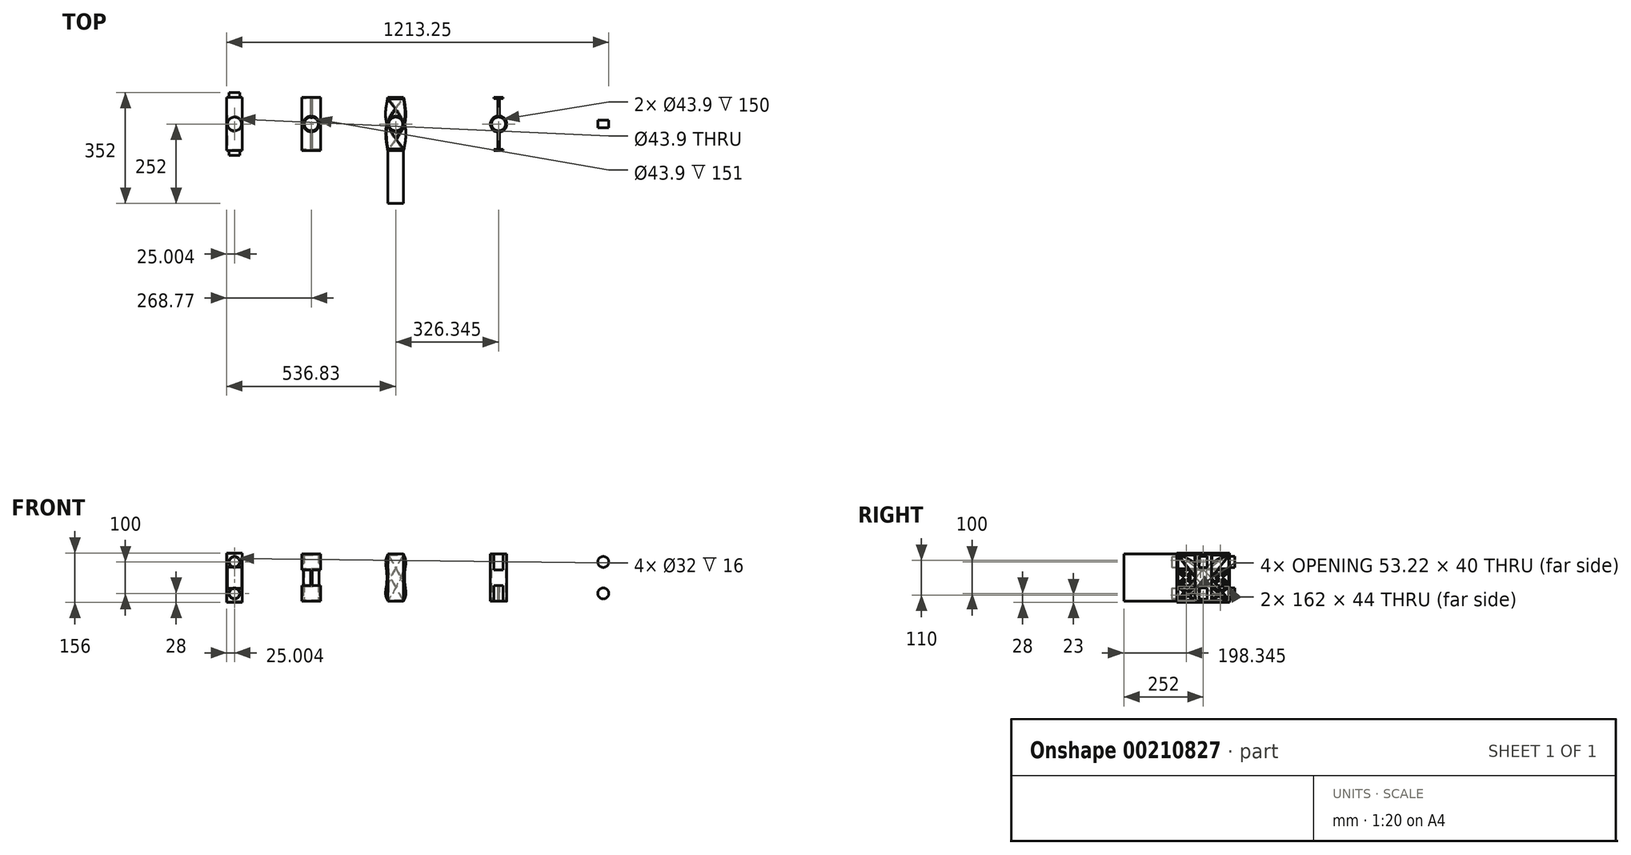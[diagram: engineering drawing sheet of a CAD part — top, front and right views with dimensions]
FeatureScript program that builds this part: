
annotation { "Feature Type Name" : "Feature", "Feature Type Description" : "" }
export const myFeature = defineFeature(function(context is Context, id is Id, definition is map)
    precondition{}
    {
        {
            var Q0;
            Q0=qCreatedBy(makeId("Top.planeOp"),FACE);
            var sketch = newSketch(context, id + "F0", { "sketchPlane" : qUnion([Q0])});
            skCircle(sketch, "E0", {"center": v(363.02, 0) * mm, "radius": 21.95 * mm});
            skCircle(sketch, "E1.0", {"center": v(363.02, 0) * mm, "radius": 25 * mm});
            skLineSegment(sketch, "E2", {"start": v(363.02, 131.9) * mm, "end": v(363.02, -84) * mm, "construction": true});
            skLineSegment(sketch, "E3", {"start": v(363.02, -84) * mm, "end": v(388.02, -84) * mm});
            skLineSegment(sketch, "E4", {"start": v(388.02, -84) * mm, "end": v(388.02, 0) * mm});
            skLineSegment(sketch, "E5.MirrorCS", {"start": v(363.02, -84) * mm, "end": v(338.02, -84) * mm});
            skLineSegment(sketch, "E6.MirrorCS", {"start": v(338.02, -84) * mm, "end": v(338.02, 0) * mm});
            skLineSegment(sketch, "E7", {"start": v(0, 0) * mm, "end": v(451.55, 0) * mm, "construction": true});
            skLineSegment(sketch, "E8.MirrorCS", {"start": v(388.02, 84) * mm, "end": v(388.02, 0) * mm});
            skLineSegment(sketch, "E9.MirrorCS", {"start": v(363.02, 84) * mm, "end": v(388.02, 84) * mm});
            skLineSegment(sketch, "E10.MirrorCS", {"start": v(363.02, 84) * mm, "end": v(338.02, 84) * mm});
            skLineSegment(sketch, "E11.MirrorCS", {"start": v(338.02, 84) * mm, "end": v(338.02, 0) * mm});
            skLineSegment(sketch, "E12.0", {"start": v(363.02, 82) * mm, "end": v(386.02, 82) * mm});
            skLineSegment(sketch, "E12.1", {"start": v(363.02, 82) * mm, "end": v(340.02, 82) * mm});
            skLineSegment(sketch, "E12.2", {"start": v(386.02, 82) * mm, "end": v(386.02, 0) * mm});
            skLineSegment(sketch, "E12.3", {"start": v(340.02, 82) * mm, "end": v(340.02, 0) * mm});
            skLineSegment(sketch, "E12.4", {"start": v(386.02, -82) * mm, "end": v(386.02, 0) * mm});
            skLineSegment(sketch, "E12.5", {"start": v(363.02, -82) * mm, "end": v(386.02, -82) * mm});
            skLineSegment(sketch, "E12.6", {"start": v(363.02, -82) * mm, "end": v(340.02, -82) * mm});
            skLineSegment(sketch, "E12.7", {"start": v(340.02, -82) * mm, "end": v(340.02, 0) * mm});
            skSolve(sketch);
        }
        {
            var Q0;
            Q0=sQuery(id+"F0.wireOp",EDGE,"E2");
            var Q1;
            Q1=sQuery(id+"F0.wireOp",VERTEX,"E5.MirrorCS.start");
            cPlane(context, id + "F1", {"entities" : qUnion([Q0, Q1]), "cplaneType" : CPlaneType.LINE_POINT, "offset" : 25 * mm, "width" : 150 * mm, "height" : 150 * mm});
        }
        {
            var Q0;
            Q0=qCreatedBy(id+"F1.planeOp",FACE);
            var sketch = newSketch(context, id + "F2", { "sketchPlane" : qUnion([Q0])});
            skLineSegment(sketch, "E13.bottom", {"start": v(338.02, 150) * mm, "end": v(388.02, 150) * mm});
            skLineSegment(sketch, "E13.top", {"start": v(338.02, 0) * mm, "end": v(388.02, 0) * mm});
            skLineSegment(sketch, "E13.left", {"start": v(338.02, 150) * mm, "end": v(338.02, 0) * mm});
            skLineSegment(sketch, "E13.right", {"start": v(388.02, 150) * mm, "end": v(388.02, 0) * mm});
            skLineSegment(sketch, "E14", {"start": v(363.02, -41.72) * mm, "end": v(363.02, 175.72) * mm, "construction": true});
            skCircle(sketch, "E15", {"center": v(363.02, 25) * mm, "radius": 17.5 * mm});
            skCircle(sketch, "E16", {"center": v(363.02, 125) * mm, "radius": 17.5 * mm});
            skSolve(sketch);
        }
        {
            var Q0;
            {var subQ0=sQuery(id+"F0.wireOp",EDGE,"E9.MirrorCS");Q0=makeQuery(id+"F0.imprint","IMPRINT",FACE,{"disambiguationData":[TD([[makeQuery(id+"F0.imprint","IMPRINT",EDGE,{"derivedFrom":subQ0}),-1.0]])]});}
            var Q1;
            Q1=makeQuery(id+"F0.imprint","IMPRINT",FACE,{"disambiguationData":[TD([[makeQuery(id+"F0.imprint","IMPRINT",EDGE,{"derivedFrom":sQuery(id+"F0.wireOp",EDGE,"E0")}),-1.0]])]});
            var Q2;
            {var subQ3=sQuery(id+"F0.wireOp",EDGE,"E1.0");var subQ7=makeQuery(id+"F0.imprint","INTERSECT",VERTEX,{"derivedFrom":[subQ3,sQuery(id+"F0.wireOp",EDGE,"E11.MirrorCS")]});Q2=makeQuery(id+"F0.imprint","IMPRINT",FACE,{"disambiguationData":[TD([[makeQuery(id+"F0.imprint","IMPRINT",EDGE,{"disambiguationData":[TD([[subQ7,1.0]])],"derivedFrom":subQ3}),1.0]])]});}
            var Q3;
            {var subQ3=sQuery(id+"F0.wireOp",EDGE,"E1.0");var subQ5=makeQuery(id+"F0.imprint","INTERSECT",VERTEX,{"derivedFrom":[subQ3,sQuery(id+"F0.wireOp",EDGE,"E8.MirrorCS")]});Q3=makeQuery(id+"F0.imprint","IMPRINT",FACE,{"disambiguationData":[TD([[makeQuery(id+"F0.imprint","IMPRINT",EDGE,{"disambiguationData":[TD([[subQ5,-1.0]])],"derivedFrom":subQ3}),1.0]])]});}
            var Q4;
            {var subQ1=sQuery(id+"F0.wireOp",EDGE,"E3");Q4=makeQuery(id+"F0.imprint","IMPRINT",FACE,{"disambiguationData":[TD([[makeQuery(id+"F0.imprint","IMPRINT",EDGE,{"derivedFrom":subQ1}),1.0]])]});}
            var Q5;
            Q5=sQuery(id+"F2.wireOp",VERTEX,"E13.left.start");
            extrude(context, id + "F3", {"entities" : qUnion([Q0, Q1, Q2, Q3, Q4]), "endBound" : BoundingType.UP_TO_VERTEX, "endBoundEntityVertex" : qUnion([Q5]), "depth" : 25 * mm});
        }
        {
            var Q0;
            Q0=makeQuery(id+"F2.imprint","IMPRINT",FACE,{"disambiguationData":[TD([[makeQuery(id+"F2.imprint","IMPRINT",EDGE,{"derivedFrom":sQuery(id+"F2.wireOp",EDGE,"E16")}),1.0]])]});
            var Q1;
            Q1=makeQuery(id+"F2.imprint","IMPRINT",FACE,{"disambiguationData":[TD([[makeQuery(id+"F2.imprint","IMPRINT",EDGE,{"derivedFrom":sQuery(id+"F2.wireOp",EDGE,"E15")}),1.0]])]});
            extrude(context, id + "F4", {"entities" : qUnion([Q0, Q1]), "depth" : 16 * mm});
        }
        {
            var Q0;
            Q0=qCreatedBy(makeId("Front.planeOp"),FACE);
            var sketch = newSketch(context, id + "F5", { "sketchPlane" : qUnion([Q0])});
            skLineSegment(sketch, "E17", {"start": v(363.02, 230.87) * mm, "end": v(363.02, -116.23) * mm, "construction": true});
            skSolve(sketch);
        }
        {
            var Q0;
            Q0=sQuery(id+"F2.wireOp",VERTEX,"E15.center");
            var Q1;
            Q1=sQuery(id+"F2.wireOp",VERTEX,"E16.center");
            var Q2;
            Q2=makeQuery(id+"F4.opExtrude","SWEPT_BODY",BODY,{"disambiguationData":[OSD([sQuery(id+"F2.wireOp",EDGE,"E16")])]});
            var Q3;
            Q3=makeQuery(id+"F4.opExtrude","SWEPT_BODY",BODY,{"disambiguationData":[OSD([sQuery(id+"F2.wireOp",EDGE,"E15")])]});
            hole(context, id + "F6", {"style" : HoleStyle.SIMPLE, "endStyle" : HoleEndStyle.THROUGH, "oppositeDirection" : true, "holeDiameter" : 32 * mm, "locations" : qUnion([Q0, Q1]), "scope" : qUnion([Q2, Q3]), "isTappedThrough" : true});
        }
        {
            var Q0;
            Q0=makeQuery(id+"F4.opExtrude","SWEPT_BODY",BODY,{"disambiguationData":[OSD([sQuery(id+"F2.wireOp",EDGE,"E16")])]});
            var Q1;
            Q1=makeQuery(id+"F4.opExtrude","SWEPT_BODY",BODY,{"disambiguationData":[OSD([sQuery(id+"F2.wireOp",EDGE,"E15")])]});
            var Q2;
            Q2=qCreatedBy(makeId("Front.planeOp"),FACE);
            mirror(context, id + "F7", {"operationType" : NewBodyOperationType.ADD, "entities" : qUnion([Q0, Q1]), "mirrorPlane" : qUnion([Q2])});
        }
        {
            var Q0;
            Q0=qCreatedBy(makeId("Top.planeOp"),FACE);
            var sketch = newSketch(context, id + "F8", { "sketchPlane" : qUnion([Q0])});
            skLineSegment(sketch, "E18", {"start": v(354.9, 0) * mm, "end": v(696.57, 0) * mm, "construction": true});
            skLineSegment(sketch, "E19", {"start": v(606.79, 88.82) * mm, "end": v(606.79, 0) * mm, "construction": true});
            skLineSegment(sketch, "E20", {"start": v(606.79, 0) * mm, "end": v(606.79, -110.58) * mm, "construction": true});
            skCircle(sketch, "E21", {"center": v(606.79, 0) * mm, "radius": 21.95 * mm});
            skCircle(sketch, "E22", {"center": v(606.79, 0) * mm, "radius": 25 * mm});
            skLineSegment(sketch, "E23.bottom", {"start": v(636.79, -84) * mm, "end": v(576.79, -84) * mm});
            skLineSegment(sketch, "E23.top", {"start": v(636.79, 84) * mm, "end": v(576.79, 84) * mm});
            skLineSegment(sketch, "E23.left", {"start": v(636.79, -84) * mm, "end": v(636.79, 84) * mm});
            skLineSegment(sketch, "E23.right", {"start": v(576.79, -84) * mm, "end": v(576.79, 84) * mm});
            skLineSegment(sketch, "E24.bottom", {"start": v(636.79, 84) * mm, "end": v(661.79, 84) * mm});
            skLineSegment(sketch, "E24.top", {"start": v(636.79, -84) * mm, "end": v(661.79, -84) * mm});
            skLineSegment(sketch, "E24.left", {"start": v(636.79, 84) * mm, "end": v(636.79, -84) * mm});
            skLineSegment(sketch, "E24.right", {"start": v(661.79, 84) * mm, "end": v(661.79, -84) * mm});
            skPoint(sketch, "E24.middle", {"position": v(649.29, 0) * mm});
            skSolve(sketch);
        }
        {
            var Q0;
            Q0=sQuery(id+"F8.wireOp",EDGE,"E23.right");
            var Q1;
            Q1=qCreatedBy(makeId("Right.planeOp"),FACE);
            cPlane(context, id + "F9", {"entities" : qUnion([Q0, Q1]), "cplaneType" : CPlaneType.LINE_ANGLE, "offset" : 25 * mm, "angle" : 0 * degree, "width" : 150 * mm, "height" : 150 * mm});
        }
        {
            var Q0;
            Q0=qCreatedBy(id+"F9.planeOp",FACE);
            var sketch = newSketch(context, id + "F10", { "sketchPlane" : qUnion([Q0])});
            skLineSegment(sketch, "E25", {"start": v(0, 0) * mm, "end": v(0, 324.05) * mm, "construction": true});
            skLineSegment(sketch, "E26.bottom", {"start": v(-84, 50) * mm, "end": v(84, 50) * mm});
            skLineSegment(sketch, "E26.top", {"start": v(-84, 0) * mm, "end": v(84, 0) * mm});
            skLineSegment(sketch, "E26.left", {"start": v(-84, 50) * mm, "end": v(-84, 0) * mm});
            skLineSegment(sketch, "E26.right", {"start": v(84, 50) * mm, "end": v(84, 0) * mm});
            skPoint(sketch, "E26.middle", {"position": v(0, 25) * mm});
            skLineSegment(sketch, "E27.bottom", {"start": v(-84, 100) * mm, "end": v(84, 100) * mm});
            skLineSegment(sketch, "E27.left", {"start": v(-84, 100) * mm, "end": v(-84, 50) * mm});
            skLineSegment(sketch, "E27.right", {"start": v(84, 100) * mm, "end": v(84, 50) * mm});
            skPoint(sketch, "E27.middle", {"position": v(0, 75) * mm});
            skLineSegment(sketch, "E28.bottom", {"start": v(-84, 150) * mm, "end": v(84, 150) * mm});
            skLineSegment(sketch, "E28.left", {"start": v(-84, 150) * mm, "end": v(-84, 100) * mm});
            skLineSegment(sketch, "E28.right", {"start": v(84, 150) * mm, "end": v(84, 100) * mm});
            skPoint(sketch, "E28.middle", {"position": v(0, 125) * mm});
            skLineSegment(sketch, "E29.bottom", {"start": v(-81, 3) * mm, "end": v(81, 3) * mm});
            skLineSegment(sketch, "E29.top", {"start": v(-81, 47) * mm, "end": v(81, 47) * mm});
            skLineSegment(sketch, "E29.left", {"start": v(-81, 3) * mm, "end": v(-81, 47) * mm});
            skLineSegment(sketch, "E29.right", {"start": v(81, 3) * mm, "end": v(81, 47) * mm});
            skLineSegment(sketch, "E30.bottom", {"start": v(-81, 103) * mm, "end": v(81, 103) * mm});
            skLineSegment(sketch, "E30.top", {"start": v(-81, 147) * mm, "end": v(81, 147) * mm});
            skLineSegment(sketch, "E30.left", {"start": v(-81, 103) * mm, "end": v(-81, 147) * mm});
            skLineSegment(sketch, "E30.right", {"start": v(81, 103) * mm, "end": v(81, 147) * mm});
            skSolve(sketch);
        }
        {
            var Q0;
            Q0=makeQuery(id+"F10.imprint","IMPRINT",FACE,{"disambiguationData":[TD([[makeQuery(id+"F10.imprint","IMPRINT",EDGE,{"derivedFrom":sQuery(id+"F10.wireOp",EDGE,"E28.bottom")}),-1.0]])]});
            var Q1;
            Q1=makeQuery(id+"F10.imprint","IMPRINT",FACE,{"disambiguationData":[TD([[makeQuery(id+"F10.imprint","IMPRINT",EDGE,{"derivedFrom":sQuery(id+"F10.wireOp",EDGE,"E26.top")}),1.0]])]});
            var Q2;
            Q2=sQuery(id+"F8.wireOp",VERTEX,"E24.top.start");
            extrude(context, id + "F11", {"entities" : qUnion([Q0, Q1]), "endBound" : BoundingType.UP_TO_VERTEX, "oppositeDirection" : true, "endBoundEntityVertex" : qUnion([Q2]), "depth" : 25 * mm});
        }
        {
            var Q0;
            Q0=makeQuery(id+"F8.imprint","IMPRINT",FACE,{"disambiguationData":[TD([[makeQuery(id+"F8.imprint","IMPRINT",EDGE,{"derivedFrom":sQuery(id+"F8.wireOp",EDGE,"E21")}),-1.0]])]});
            var Q1;
            Q1=makeQuery(id+"F11.opExtrude","CAP_VERTEX",VERTEX,{"disambiguationData":[OSD([sQuery(id+"F10.wireOp",EDGE,"E28.bottom"),sQuery(id+"F10.wireOp",EDGE,"E28.right"),dummyQuery(id+"F11.vertexPlane.planeOp",FACE)])],"isStart":false});
            extrude(context, id + "F12", {"entities" : qUnion([Q0]), "operationType" : NewBodyOperationType.ADD, "endBoundEntityVertex" : qUnion([Q1]), "depth" : 151 * mm});
        }
        {
            var Q0;
            Q0=makeQuery(id+"F8.imprint","IMPRINT",FACE,{"disambiguationData":[TD([[makeQuery(id+"F8.imprint","IMPRINT",EDGE,{"derivedFrom":sQuery(id+"F8.wireOp",EDGE,"E21")}),1.0]])]});
            extrude(context, id + "F13", {"entities" : qUnion([Q0]), "operationType" : NewBodyOperationType.REMOVE, "depth" : 151 * mm});
        }
        {
            var Q0;
            Q0=sQuery(id+"F8.wireOp",EDGE,"E20");
            var Q1;
            Q1=qCreatedBy(makeId("Right.planeOp"),FACE);
            cPlane(context, id + "F14", {"entities" : qUnion([Q0, Q1]), "cplaneType" : CPlaneType.LINE_ANGLE, "offset" : 25 * mm, "angle" : 0 * degree, "width" : 150 * mm, "height" : 150 * mm});
        }
        {
            var Q0;
            Q0=qCreatedBy(id+"F14.planeOp",FACE);
            var sketch = newSketch(context, id + "F15", { "sketchPlane" : qUnion([Q0])});
            skLineSegment(sketch, "E31", {"start": v(84, 100) * mm, "end": v(23.18, 48.45) * mm, "construction": true});
            skLineSegment(sketch, "E32", {"start": v(84, 50) * mm, "end": v(23.18, 104.08) * mm, "construction": true});
            skLineSegment(sketch, "E33", {"start": v(84, 100) * mm, "end": v(79, 100) * mm});
            skLineSegment(sketch, "E34", {"start": v(79, 100) * mm, "end": v(55.65, 80.2) * mm});
            skLineSegment(sketch, "E35", {"start": v(55.65, 80.2) * mm, "end": v(33.39, 100) * mm});
            skLineSegment(sketch, "E36", {"start": v(33.39, 100) * mm, "end": v(22.77, 100) * mm});
            skLineSegment(sketch, "E37", {"start": v(22.77, 100) * mm, "end": v(50.2, 75.6) * mm});
            skLineSegment(sketch, "E38", {"start": v(50.2, 75.6) * mm, "end": v(20, 50) * mm});
            skLineSegment(sketch, "E39", {"start": v(20, 50) * mm, "end": v(30.9, 50) * mm});
            skLineSegment(sketch, "E40", {"start": v(30.9, 50) * mm, "end": v(55.53, 70.87) * mm});
            skLineSegment(sketch, "E41", {"start": v(55.53, 70.87) * mm, "end": v(79, 50) * mm});
            skLineSegment(sketch, "E42", {"start": v(79, 50) * mm, "end": v(84, 50) * mm});
            skLineSegment(sketch, "E43", {"start": v(84, 50) * mm, "end": v(84, 55) * mm});
            skLineSegment(sketch, "E44", {"start": v(84, 55) * mm, "end": v(60.97, 75.48) * mm});
            skLineSegment(sketch, "E45", {"start": v(60.97, 75.48) * mm, "end": v(84, 95) * mm});
            skLineSegment(sketch, "E46", {"start": v(84, 95) * mm, "end": v(84, 100) * mm});
            skSolve(sketch);
        }
        {
            var Q0;
            Q0=makeQuery(id+"F15.imprint","IMPRINT",FACE,{"disambiguationData":[TD([[makeQuery(id+"F15.imprint","IMPRINT",EDGE,{"derivedFrom":sQuery(id+"F15.wireOp",EDGE,"E33")}),1.0]])]});
            extrude(context, id + "F16", {"entities" : qUnion([Q0]), "endBound" : BoundingType.SYMMETRIC, "depth" : 5 * mm});
        }
        {
            var Q0;
            Q0=makeQuery(id+"F16.opExtrude","SWEPT_BODY",BODY,{"disambiguationData":[OSD([sQuery(id+"F15.wireOp",EDGE,"E33"),sQuery(id+"F15.wireOp",EDGE,"E34"),sQuery(id+"F15.wireOp",EDGE,"E35"),sQuery(id+"F15.wireOp",EDGE,"E36"),sQuery(id+"F15.wireOp",EDGE,"E37"),sQuery(id+"F15.wireOp",EDGE,"E38"),sQuery(id+"F15.wireOp",EDGE,"E39"),sQuery(id+"F15.wireOp",EDGE,"E40"),sQuery(id+"F15.wireOp",EDGE,"E41"),sQuery(id+"F15.wireOp",EDGE,"E42"),sQuery(id+"F15.wireOp",EDGE,"E43"),sQuery(id+"F15.wireOp",EDGE,"E44"),sQuery(id+"F15.wireOp",EDGE,"E45"),sQuery(id+"F15.wireOp",EDGE,"E46")])]});
            var Q1;
            Q1=qCreatedBy(makeId("Front.planeOp"),FACE);
            mirror(context, id + "F17", {"operationType" : NewBodyOperationType.ADD, "entities" : qUnion([Q0]), "mirrorPlane" : qUnion([Q1])});
        }
        {
            var Q0;
            Q0=qCreatedBy(makeId("Top.planeOp"),FACE);
            var sketch = newSketch(context, id + "F18", { "sketchPlane" : qUnion([Q0])});
            skLineSegment(sketch, "E47", {"start": v(582.23, 0) * mm, "end": v(967.92, 0) * mm, "construction": true});
            skLineSegment(sketch, "E48", {"start": v(874.85, 115.5) * mm, "end": v(874.85, -115.5) * mm, "construction": true});
            skCircle(sketch, "E49", {"center": v(874.85, 0) * mm, "radius": 21.95 * mm});
            skCircle(sketch, "E50", {"center": v(874.85, 0) * mm, "radius": 25 * mm});
            skLineSegment(sketch, "E51.bottom", {"start": v(899.85, -84) * mm, "end": v(849.85, -84) * mm});
            skLineSegment(sketch, "E51.top", {"start": v(899.85, 84) * mm, "end": v(849.85, 84) * mm});
            skLineSegment(sketch, "E51.left", {"start": v(899.85, -84) * mm, "end": v(899.85, 84) * mm});
            skLineSegment(sketch, "E51.right", {"start": v(849.85, -84) * mm, "end": v(849.85, 84) * mm});
            skLineSegment(sketch, "E52", {"start": v(849.85, 81) * mm, "end": v(899.85, 81) * mm});
            skLineSegment(sketch, "E53", {"start": v(849.85, -81) * mm, "end": v(899.85, -81) * mm});
            skSolve(sketch);
        }
        {
            var Q0;
            {var subQ5=sQuery(id+"F18.wireOp",EDGE,"E53");Q0=makeQuery(id+"F18.imprint","IMPRINT",FACE,{"disambiguationData":[TD([[makeQuery(id+"F18.imprint","IMPRINT",EDGE,{"derivedFrom":subQ5}),1.0]])]});}
            cPlane(context, id + "F19", {"entities" : qUnion([Q0]), "cplaneType" : CPlaneType.OFFSET, "offset" : 150 * mm, "width" : 150 * mm, "height" : 150 * mm});
        }
        {
            var Q0;
            Q0=qCreatedBy(id+"F19.planeOp",FACE);
            var sketch = newSketch(context, id + "F20", { "sketchPlane" : qUnion([Q0])});
            skLineSegment(sketch, "E54", {"start": v(874.85, 115.5) * mm, "end": v(874.85, -115.5) * mm, "construction": true});
            skCircle(sketch, "E55", {"center": v(874.85, 0) * mm, "radius": 21.95 * mm});
            skCircle(sketch, "E56", {"center": v(874.85, 0) * mm, "radius": 25 * mm});
            skLineSegment(sketch, "E57.bottom", {"start": v(899.85, -84) * mm, "end": v(849.85, -84) * mm});
            skLineSegment(sketch, "E57.top", {"start": v(899.85, 84) * mm, "end": v(849.85, 84) * mm});
            skLineSegment(sketch, "E57.left", {"start": v(899.85, -84) * mm, "end": v(899.85, 84) * mm});
            skLineSegment(sketch, "E57.right", {"start": v(849.85, -84) * mm, "end": v(849.85, 84) * mm});
            skLineSegment(sketch, "E58", {"start": v(849.85, 79) * mm, "end": v(899.85, 79) * mm});
            skLineSegment(sketch, "E59", {"start": v(849.85, -79) * mm, "end": v(899.85, -79) * mm});
            skSolve(sketch);
        }
        {
            var Q0;
            Q0=makeQuery(id+"F18.imprint","IMPRINT",FACE,{"disambiguationData":[TD([[makeQuery(id+"F18.imprint","IMPRINT",EDGE,{"derivedFrom":sQuery(id+"F18.wireOp",EDGE,"E49")}),-1.0]])]});
            var Q1;
            Q1=qCreatedBy(id+"F19.planeOp",FACE);
            extrude(context, id + "F21", {"entities" : qUnion([Q0]), "endBound" : BoundingType.UP_TO_SURFACE, "endBoundEntityFace" : qUnion([Q1]), "depth" : 25 * mm});
        }
        {
            var Q0;
            Q0=sQuery(id+"F20.wireOp",EDGE,"E57.left");
            var Q1;
            Q1=qCreatedBy(makeId("Right.planeOp"),FACE);
            cPlane(context, id + "F22", {"entities" : qUnion([Q0, Q1]), "cplaneType" : CPlaneType.LINE_ANGLE, "offset" : 25 * mm, "angle" : 0 * degree, "width" : 150 * mm, "height" : 150 * mm});
        }
        {
            var Q0;
            Q0=qCreatedBy(id+"F22.planeOp",FACE);
            var sketch = newSketch(context, id + "F23", { "sketchPlane" : qUnion([Q0])});
            skLineSegment(sketch, "E60", {"start": v(0, 0) * mm, "end": v(0, 50) * mm});
            skLineSegment(sketch, "E61", {"start": v(0, 100) * mm, "end": v(0, 150) * mm});
            skLineSegment(sketch, "E62", {"start": v(0, 50) * mm, "end": v(0, 100) * mm});
            skSolve(sketch);
        }
        {
            var Q0;
            Q0=sQuery(id+"F23.wireOp",EDGE,"E62");
            var Q1;
            Q1=qCreatedBy(makeId("Front.planeOp"),FACE);
            cPlane(context, id + "F24", {"entities" : qUnion([Q0, Q1]), "cplaneType" : CPlaneType.LINE_ANGLE, "offset" : 25 * mm, "angle" : 0 * degree, "width" : 150 * mm, "height" : 150 * mm});
        }
        {
            var Q0;
            Q0=qCreatedBy(id+"F24.planeOp",FACE);
            var sketch = newSketch(context, id + "F25", { "sketchPlane" : qUnion([Q0])});
            skLineSegment(sketch, "E63.bottom", {"start": v(-899.85, 100) * mm, "end": v(-902.85, 100) * mm});
            skLineSegment(sketch, "E63.top", {"start": v(-899.85, 50) * mm, "end": v(-902.85, 50) * mm});
            skLineSegment(sketch, "E63.left", {"start": v(-899.85, 100) * mm, "end": v(-899.85, 50) * mm});
            skLineSegment(sketch, "E63.right", {"start": v(-902.85, 100) * mm, "end": v(-902.85, 50) * mm});
            skSolve(sketch);
        }
        {
            var Q1;
            {var subQ0=sQuery(id+"F20.wireOp",EDGE,"E57.top");Q1=makeQuery(id+"F20.imprint","IMPRINT",FACE,{"disambiguationData":[TD([[makeQuery(id+"F20.imprint","IMPRINT",EDGE,{"derivedFrom":subQ0}),1.0]])]});}
            var Q2;
            Q2=makeQuery(id+"F25.imprint","IMPRINT",FACE,{"disambiguationData":[TD([[makeQuery(id+"F25.imprint","IMPRINT",EDGE,{"derivedFrom":sQuery(id+"F25.wireOp",EDGE,"E63.bottom")}),1.0]])]});
            var Q3;
            {var subQ0=sQuery(id+"F18.wireOp",EDGE,"E51.bottom");Q3=makeQuery(id+"F18.imprint","IMPRINT",FACE,{"disambiguationData":[TD([[makeQuery(id+"F18.imprint","IMPRINT",EDGE,{"derivedFrom":subQ0}),-1.0]])]});}
            loft(context, id + "F26", {"sheetProfilesArray" : [{ "sheetProfileEntities" : qUnion([Q1]) }, { "sheetProfileEntities" : qUnion([Q2]) }, { "sheetProfileEntities" : qUnion([Q3]) }]});
        }
        {
            var Q0;
            {var subQ0=sQuery(id+"F20.wireOp",EDGE,"E57.top");var subQ4=sQuery(id+"F18.wireOp",EDGE,"E51.bottom");Q0=makeQuery(id+"F26.opLoft","SWEPT_BODY",BODY,{"disambiguationData":[OSD([makeQuery(id+"F18.imprint","IMPRINT",FACE,{"disambiguationData":[TD([[makeQuery(id+"F18.imprint","IMPRINT",EDGE,{"derivedFrom":subQ4}),-1.0]])]}),makeQuery(id+"F20.imprint","IMPRINT",FACE,{"disambiguationData":[TD([[makeQuery(id+"F20.imprint","IMPRINT",EDGE,{"derivedFrom":subQ0}),1.0]])]}),sQuery(id+"F25.wireOp",EDGE,"E63.bottom")])]});}
            transform(context, id + "F27", {"entities" : qUnion([Q0]), "transformType" : TransformType.COPY});
        }
        {
            var Q0;
            {var subQ0=sQuery(id+"F20.wireOp",EDGE,"E57.top");var subQ4=sQuery(id+"F18.wireOp",EDGE,"E51.bottom");Q0=makeQuery(id+"F27.opPattern","COPY",BODY,{"derivedFrom":makeQuery(id+"F26.opLoft","SWEPT_BODY",BODY,{"disambiguationData":[OSD([makeQuery(id+"F18.imprint","IMPRINT",FACE,{"disambiguationData":[TD([[makeQuery(id+"F18.imprint","IMPRINT",EDGE,{"derivedFrom":subQ4}),-1.0]])]}),makeQuery(id+"F20.imprint","IMPRINT",FACE,{"disambiguationData":[TD([[makeQuery(id+"F20.imprint","IMPRINT",EDGE,{"derivedFrom":subQ0}),1.0]])]}),sQuery(id+"F25.wireOp",EDGE,"E63.bottom")])]}),"instanceName":"1"});}
            var Q1;
            Q1=sQuery(id+"F23.wireOp",EDGE,"E62");
            transform(context, id + "F28", {"entities" : qUnion([Q0]), "transformType" : TransformType.ROTATION, "transformAxis" : qUnion([Q1]), "angle" : 180 * degree, "makeCopy" : false});
        }
        {
            var Q0;
            {var subQ0=sQuery(id+"F20.wireOp",EDGE,"E57.top");var subQ4=sQuery(id+"F18.wireOp",EDGE,"E51.bottom");Q0=makeQuery(id+"F27.opPattern","COPY",BODY,{"derivedFrom":makeQuery(id+"F26.opLoft","SWEPT_BODY",BODY,{"disambiguationData":[OSD([makeQuery(id+"F18.imprint","IMPRINT",FACE,{"disambiguationData":[TD([[makeQuery(id+"F18.imprint","IMPRINT",EDGE,{"derivedFrom":subQ4}),-1.0]])]}),makeQuery(id+"F20.imprint","IMPRINT",FACE,{"disambiguationData":[TD([[makeQuery(id+"F20.imprint","IMPRINT",EDGE,{"derivedFrom":subQ0}),1.0]])]}),sQuery(id+"F25.wireOp",EDGE,"E63.bottom")])]}),"instanceName":"1"});}
            transform(context, id + "F29", {"entities" : qUnion([Q0]), "transformType" : TransformType.TRANSLATION_3D, "dx" : -50 * mm, "dy" : 0 * mm, "dz" : 0 * mm, "makeCopy" : false});
        }
        {
            var Q0;
            {var subQ0=sQuery(id+"F18.wireOp",EDGE,"E51.bottom");Q0=makeQuery(id+"F18.imprint","IMPRINT",FACE,{"disambiguationData":[TD([[makeQuery(id+"F18.imprint","IMPRINT",EDGE,{"derivedFrom":subQ0}),-1.0]])]});}
            var Q1;
            {var subQ0=sQuery(id+"F18.wireOp",EDGE,"E51.top");Q1=makeQuery(id+"F18.imprint","IMPRINT",FACE,{"disambiguationData":[TD([[makeQuery(id+"F18.imprint","IMPRINT",EDGE,{"derivedFrom":subQ0}),1.0]])]});}
            var Q2;
            Q2=qCreatedBy(id+"F19.planeOp",FACE);
            extrude(context, id + "F30", {"entities" : qUnion([Q0, Q1]), "operationType" : NewBodyOperationType.ADD, "endBound" : BoundingType.UP_TO_SURFACE, "endBoundEntityFace" : qUnion([Q2]), "depth" : 25 * mm});
        }
        {
            var Q0;
            Q0=qCreatedBy(makeId("Top.planeOp"),FACE);
            var sketch = newSketch(context, id + "F31", { "sketchPlane" : qUnion([Q0])});
            skLineSegment(sketch, "E64", {"start": v(575.98, 0) * mm, "end": v(1360.94, 0) * mm, "construction": true});
            skCircle(sketch, "E65", {"center": v(1201.2, 0) * mm, "radius": 21.95 * mm});
            skLineSegment(sketch, "E66", {"start": v(1201.2, 68.58) * mm, "end": v(1201.2, -89.25) * mm, "construction": true});
            skCircle(sketch, "E67", {"center": v(1201.2, 0) * mm, "radius": 26 * mm});
            skSolve(sketch);
        }
        {
            var Q0;
            Q0=sQuery(id+"F31.wireOp",EDGE,"E66");
            var Q1;
            Q1=qCreatedBy(makeId("Right.planeOp"),FACE);
            cPlane(context, id + "F32", {"entities" : qUnion([Q0, Q1]), "cplaneType" : CPlaneType.LINE_ANGLE, "offset" : 25 * mm, "angle" : 0 * degree, "width" : 150 * mm, "height" : 150 * mm});
        }
        {
            var Q0;
            Q0=qCreatedBy(id+"F32.planeOp",FACE);
            var sketch = newSketch(context, id + "F33", { "sketchPlane" : qUnion([Q0])});
            skLineSegment(sketch, "E68.bottom", {"start": v(84, 0) * mm, "end": v(81, 0) * mm});
            skLineSegment(sketch, "E68.top", {"start": v(84, 50) * mm, "end": v(-84, 50) * mm});
            skLineSegment(sketch, "E68.left", {"start": v(84, 0) * mm, "end": v(84, 50) * mm});
            skLineSegment(sketch, "E68.right", {"start": v(-84, 0) * mm, "end": v(-84, 50) * mm});
            skLineSegment(sketch, "E69.top", {"start": v(84, 100) * mm, "end": v(-84, 100) * mm});
            skLineSegment(sketch, "E69.left", {"start": v(84, 50) * mm, "end": v(84, 100) * mm});
            skLineSegment(sketch, "E69.right", {"start": v(-84, 50) * mm, "end": v(-84, 100) * mm});
            skLineSegment(sketch, "E70.bottom", {"start": v(84, 100) * mm, "end": v(29.54, 100) * mm});
            skLineSegment(sketch, "E70.top", {"start": v(84, 150) * mm, "end": v(-84, 150) * mm});
            skLineSegment(sketch, "E70.left", {"start": v(84, 100) * mm, "end": v(84, 150) * mm});
            skLineSegment(sketch, "E70.right", {"start": v(-84, 100) * mm, "end": v(-84, 150) * mm});
            skLineSegment(sketch, "E71", {"start": v(81, 150) * mm, "end": v(81, 103.54) * mm});
            skLineSegment(sketch, "E72", {"start": v(-81, 150) * mm, "end": v(-81, 0) * mm});
            skLineSegment(sketch, "E73", {"start": v(81, 0) * mm, "end": v(-81, 0) * mm});
            skLineSegment(sketch, "E74", {"start": v(-81, 0) * mm, "end": v(-84, 0) * mm});
            skLineSegment(sketch, "E75", {"start": v(-26, 0) * mm, "end": v(-26, 150) * mm});
            skLineSegment(sketch, "E76", {"start": v(26, 0) * mm, "end": v(26, 146.46) * mm});
            skLineSegment(sketch, "E77", {"start": v(81, 150) * mm, "end": v(26, 100) * mm, "construction": true});
            skLineSegment(sketch, "E78", {"start": v(26, 100) * mm, "end": v(81, 50) * mm, "construction": true});
            skLineSegment(sketch, "E79", {"start": v(81, 50) * mm, "end": v(26, 0) * mm, "construction": true});
            skLineSegment(sketch, "E80", {"start": v(81, 0) * mm, "end": v(26, 50) * mm, "construction": true});
            skLineSegment(sketch, "E81", {"start": v(26, 50) * mm, "end": v(81, 100) * mm, "construction": true});
            skLineSegment(sketch, "E82", {"start": v(81, 100) * mm, "end": v(26, 150) * mm, "construction": true});
            skLineSegment(sketch, "E83", {"start": v(-26, 150) * mm, "end": v(-81, 100) * mm, "construction": true});
            skLineSegment(sketch, "E84", {"start": v(-81, 100) * mm, "end": v(-26, 50) * mm, "construction": true});
            skLineSegment(sketch, "E85", {"start": v(-26, 50) * mm, "end": v(-81, 0) * mm, "construction": true});
            skLineSegment(sketch, "E86", {"start": v(-26, 0) * mm, "end": v(-81, 50) * mm, "construction": true});
            skLineSegment(sketch, "E87", {"start": v(-81, 50) * mm, "end": v(-26, 100) * mm, "construction": true});
            skLineSegment(sketch, "E88", {"start": v(-26, 100) * mm, "end": v(-81, 150) * mm, "construction": true});
            skLineSegment(sketch, "E89", {"start": v(81, 150) * mm, "end": v(77.46, 150) * mm});
            skLineSegment(sketch, "E90", {"start": v(77.46, 150) * mm, "end": v(53.5, 128.22) * mm});
            skLineSegment(sketch, "E91", {"start": v(53.5, 128.22) * mm, "end": v(29.54, 150) * mm});
            skLineSegment(sketch, "E92", {"start": v(29.54, 150) * mm, "end": v(26, 150) * mm});
            skLineSegment(sketch, "E93", {"start": v(26, 146.46) * mm, "end": v(49.6, 125) * mm});
            skLineSegment(sketch, "E94", {"start": v(49.6, 125) * mm, "end": v(26, 103.54) * mm});
            skLineSegment(sketch, "E95", {"start": v(26, 103.54) * mm, "end": v(26, 100) * mm});
            skLineSegment(sketch, "E96", {"start": v(29.54, 100) * mm, "end": v(53.5, 121.78) * mm});
            skLineSegment(sketch, "E97", {"start": v(53.5, 121.78) * mm, "end": v(77.46, 100) * mm});
            skLineSegment(sketch, "E98", {"start": v(77.46, 100) * mm, "end": v(81, 100) * mm});
            skLineSegment(sketch, "E99", {"start": v(81, 103.54) * mm, "end": v(57.4, 125) * mm});
            skLineSegment(sketch, "E100", {"start": v(57.4, 125) * mm, "end": v(81, 146.46) * mm});
            skLineSegment(sketch, "E101", {"start": v(81, 146.46) * mm, "end": v(81, 150) * mm});
            skLineSegment(sketch, "E102", {"start": v(81, 103.54) * mm, "end": v(81, 100) * mm});
            skLineSegment(sketch, "E103", {"start": v(29.54, 100) * mm, "end": v(26, 100) * mm});
            skLineSegment(sketch, "E104", {"start": v(26, 146.46) * mm, "end": v(26, 150) * mm});
            skLineSegment(sketch, "E105", {"start": v(81, 100) * mm, "end": v(81, 0) * mm});
            skLineSegment(sketch, "E106", {"start": v(26, 100) * mm, "end": v(-84, 100) * mm});
            skLineSegment(sketch, "E107.0.1.0", {"start": v(53.5, 78.22) * mm, "end": v(29.54, 100) * mm});
            skLineSegment(sketch, "E107.0.1.1", {"start": v(77.46, 100) * mm, "end": v(53.5, 78.22) * mm});
            skLineSegment(sketch, "E107.0.1.2", {"start": v(57.4, 75) * mm, "end": v(81, 96.46) * mm});
            skLineSegment(sketch, "E107.0.1.3", {"start": v(81, 53.54) * mm, "end": v(57.4, 75) * mm});
            skLineSegment(sketch, "E107.0.1.4", {"start": v(53.5, 71.78) * mm, "end": v(77.46, 50) * mm});
            skLineSegment(sketch, "E107.0.1.5", {"start": v(29.54, 50) * mm, "end": v(53.5, 71.78) * mm});
            skLineSegment(sketch, "E107.0.1.6", {"start": v(49.6, 75) * mm, "end": v(26, 53.54) * mm});
            skLineSegment(sketch, "E107.0.1.7", {"start": v(26, 96.46) * mm, "end": v(49.6, 75) * mm});
            skLineSegment(sketch, "E107.0.2.0", {"start": v(53.5, 28.22) * mm, "end": v(29.54, 50) * mm});
            skLineSegment(sketch, "E107.0.2.1", {"start": v(77.46, 50) * mm, "end": v(53.5, 28.22) * mm});
            skLineSegment(sketch, "E107.0.2.2", {"start": v(57.4, 25) * mm, "end": v(81, 46.46) * mm});
            skLineSegment(sketch, "E107.0.2.3", {"start": v(81, 3.54) * mm, "end": v(57.4, 25) * mm});
            skLineSegment(sketch, "E107.0.2.4", {"start": v(53.5, 21.78) * mm, "end": v(77.46, 0) * mm});
            skLineSegment(sketch, "E107.0.2.5", {"start": v(29.54, 0) * mm, "end": v(53.5, 21.78) * mm});
            skLineSegment(sketch, "E107.0.2.6", {"start": v(49.6, 25) * mm, "end": v(26, 3.54) * mm});
            skLineSegment(sketch, "E107.0.2.7", {"start": v(26, 46.46) * mm, "end": v(49.6, 25) * mm});
            skLineSegment(sketch, "E107.direction1", {"start": v(29.54, 150) * mm, "end": v(53.54, 150) * mm, "construction": true});
            skLineSegment(sketch, "E107.direction2", {"start": v(29.54, 150) * mm, "end": v(29.54, 100) * mm, "construction": true});
            skSolve(sketch);
        }
        {
            var Q0;
            Q0=makeQuery(id+"F33.imprint","IMPRINT",FACE,{"disambiguationData":[TD([[makeQuery(id+"F33.imprint","IMPRINT",EDGE,{"derivedFrom":sQuery(id+"F33.wireOp",EDGE,"E89")}),1.0]])]});
            var Q1;
            {var subQ4=sQuery(id+"F33.wireOp",EDGE,"E98");Q1=makeQuery(id+"F33.imprint","IMPRINT",FACE,{"disambiguationData":[TD([[makeQuery(id+"F33.imprint","IMPRINT",EDGE,{"derivedFrom":subQ4}),-1.0]])]});}
            var Q2;
            {var subQ9=sQuery(id+"F33.wireOp",EDGE,"E107.0.2.0");Q2=makeQuery(id+"F33.imprint","IMPRINT",FACE,{"disambiguationData":[TD([[makeQuery(id+"F33.imprint","IMPRINT",EDGE,{"derivedFrom":subQ9}),1.0]])]});}
            extrude(context, id + "F34", {"entities" : qUnion([Q0, Q1, Q2]), "endBound" : BoundingType.SYMMETRIC, "depth" : 5 * mm});
        }
        {
            var Q0;
            {var subQ1=sQuery(id+"F33.wireOp",EDGE,"E70.left");Q0=makeQuery(id+"F33.imprint","IMPRINT",FACE,{"disambiguationData":[TD([[makeQuery(id+"F33.imprint","IMPRINT",EDGE,{"derivedFrom":subQ1}),1.0]])]});}
            var Q1;
            {var subQ5=sQuery(id+"F33.wireOp",EDGE,"E68.bottom");Q1=makeQuery(id+"F33.imprint","IMPRINT",FACE,{"disambiguationData":[TD([[makeQuery(id+"F33.imprint","IMPRINT",EDGE,{"derivedFrom":subQ5}),-1.0]])]});}
            extrude(context, id + "F35", {"entities" : qUnion([Q0, Q1]), "operationType" : NewBodyOperationType.ADD, "endBound" : BoundingType.SYMMETRIC, "depth" : 30 * mm});
        }
        {
            var Q0;
            Q0=makeQuery(id+"F34.opExtrude","SWEPT_BODY",BODY,{"disambiguationData":[OSD([sQuery(id+"F33.wireOp",EDGE,"E73"),sQuery(id+"F33.wireOp",EDGE,"E76"),sQuery(id+"F33.wireOp",EDGE,"E89"),sQuery(id+"F33.wireOp",EDGE,"E90"),sQuery(id+"F33.wireOp",EDGE,"E91"),sQuery(id+"F33.wireOp",EDGE,"E92"),sQuery(id+"F33.wireOp",EDGE,"E93"),sQuery(id+"F33.wireOp",EDGE,"E94"),sQuery(id+"F33.wireOp",EDGE,"E95"),sQuery(id+"F33.wireOp",EDGE,"E96"),sQuery(id+"F33.wireOp",EDGE,"E97"),sQuery(id+"F33.wireOp",EDGE,"E99"),sQuery(id+"F33.wireOp",EDGE,"E100"),sQuery(id+"F33.wireOp",EDGE,"E101"),sQuery(id+"F33.wireOp",EDGE,"E102"),sQuery(id+"F33.wireOp",EDGE,"E104"),sQuery(id+"F33.wireOp",EDGE,"E105"),sQuery(id+"F33.wireOp",EDGE,"E107.0.1.0"),sQuery(id+"F33.wireOp",EDGE,"E107.0.1.1"),sQuery(id+"F33.wireOp",EDGE,"E107.0.1.2"),sQuery(id+"F33.wireOp",EDGE,"E107.0.1.3"),sQuery(id+"F33.wireOp",EDGE,"E107.0.1.4"),sQuery(id+"F33.wireOp",EDGE,"E107.0.1.5"),sQuery(id+"F33.wireOp",EDGE,"E107.0.1.6"),sQuery(id+"F33.wireOp",EDGE,"E107.0.1.7"),sQuery(id+"F33.wireOp",EDGE,"E107.0.2.0"),sQuery(id+"F33.wireOp",EDGE,"E107.0.2.1"),sQuery(id+"F33.wireOp",EDGE,"E107.0.2.2"),sQuery(id+"F33.wireOp",EDGE,"E107.0.2.3"),sQuery(id+"F33.wireOp",EDGE,"E107.0.2.4"),sQuery(id+"F33.wireOp",EDGE,"E107.0.2.5"),sQuery(id+"F33.wireOp",EDGE,"E107.0.2.6"),sQuery(id+"F33.wireOp",EDGE,"E107.0.2.7")])]});
            var Q1;
            Q1=qCreatedBy(makeId("Front.planeOp"),FACE);
            mirror(context, id + "F36", {"entities" : qUnion([Q0]), "mirrorPlane" : qUnion([Q1])});
        }
        {
            var Q0;
            Q0=makeQuery(id+"F31.imprint","IMPRINT",FACE,{"disambiguationData":[TD([[makeQuery(id+"F31.imprint","IMPRINT",EDGE,{"derivedFrom":sQuery(id+"F31.wireOp",EDGE,"E65")}),-1.0]])]});
            extrude(context, id + "F37", {"entities" : qUnion([Q0]), "depth" : 150 * mm});
        }
        {
            var Q0;
            Q0 = qBodyType(qCreatedBy(id + "F5" ,EDGE), BodyType.WIRE);
            var Q1;
            Q1=qCreatedBy(makeId("Right.planeOp"),FACE);
            cPlane(context, id + "F38", {"entities" : qUnion([Q0, Q1]), "cplaneType" : CPlaneType.LINE_ANGLE, "offset" : 25 * mm, "angle" : 0 * degree, "width" : 150 * mm, "height" : 150 * mm});
        }
        {
            var Q0;
            Q0=qCreatedBy(id+"F38.planeOp",FACE);
            var sketch = newSketch(context, id + "F39", { "sketchPlane" : qUnion([Q0])});
            skLineSegment(sketch, "E108.bottom", {"start": v(84, 150) * mm, "end": v(-84, 150) * mm});
            skLineSegment(sketch, "E108.top", {"start": v(84, 0) * mm, "end": v(-84, 0) * mm});
            skLineSegment(sketch, "E108.left", {"start": v(84, 150) * mm, "end": v(84, 0) * mm});
            skLineSegment(sketch, "E108.right", {"start": v(-84, 150) * mm, "end": v(-84, 0) * mm});
            skLineSegment(sketch, "E109", {"start": v(27.05, 150) * mm, "end": v(27.05, 110) * mm});
            skLineSegment(sketch, "E110", {"start": v(27.05, 110) * mm, "end": v(80.26, 150) * mm});
            skLineSegment(sketch, "E111", {"start": v(80.26, 150) * mm, "end": v(27.05, 150) * mm});
            skLineSegment(sketch, "E112", {"start": v(84, 40) * mm, "end": v(37.92, 75) * mm});
            skLineSegment(sketch, "E113", {"start": v(37.92, 75) * mm, "end": v(84, 110) * mm});
            skLineSegment(sketch, "E114", {"start": v(84, 110) * mm, "end": v(84, 40) * mm});
            skLineSegment(sketch, "E115", {"start": v(27.05, 40) * mm, "end": v(27.05, 0) * mm});
            skLineSegment(sketch, "E116", {"start": v(27.05, 0) * mm, "end": v(80.26, 0) * mm});
            skLineSegment(sketch, "E117", {"start": v(80.26, 0) * mm, "end": v(27.05, 40) * mm});
            skLineSegment(sketch, "E118", {"start": v(156.14, 75) * mm, "end": v(-157.32, 75) * mm, "construction": true});
            skLineSegment(sketch, "E119", {"start": v(159.72, 110) * mm, "end": v(-151.6, 110) * mm, "construction": true});
            skLineSegment(sketch, "E120", {"start": v(160.45, 40) * mm, "end": v(-174.15, 40) * mm, "construction": true});
            skLineSegment(sketch, "E121.MirrorCS", {"start": v(-80.26, 150) * mm, "end": v(-27.05, 150) * mm});
            skLineSegment(sketch, "E122.MirrorCS", {"start": v(-27.05, 110) * mm, "end": v(-80.26, 150) * mm});
            skLineSegment(sketch, "E123.MirrorCS", {"start": v(-27.05, 150) * mm, "end": v(-27.05, 110) * mm});
            skLineSegment(sketch, "E124.MirrorCS", {"start": v(-37.92, 75) * mm, "end": v(-84, 110) * mm});
            skLineSegment(sketch, "E125.MirrorCS", {"start": v(-84, 40) * mm, "end": v(-37.92, 75) * mm});
            skLineSegment(sketch, "E126.MirrorCS", {"start": v(-80.26, 0) * mm, "end": v(-27.05, 40) * mm});
            skLineSegment(sketch, "E127.MirrorCS", {"start": v(-27.05, 40) * mm, "end": v(-27.05, 0) * mm});
            skSolve(sketch);
        }
        {
            var Q0;
            Q0=makeQuery(id+"F39.imprint","IMPRINT",FACE,{"disambiguationData":[TD([[makeQuery(id+"F39.imprint","IMPRINT",EDGE,{"derivedFrom":sQuery(id+"F39.wireOp",EDGE,"E109")}),1.0]])]});
            var Q1;
            Q1=makeQuery(id+"F39.imprint","IMPRINT",FACE,{"disambiguationData":[TD([[makeQuery(id+"F39.imprint","IMPRINT",EDGE,{"derivedFrom":sQuery(id+"F39.wireOp",EDGE,"E121.MirrorCS")}),-1.0]])]});
            var Q2;
            {var subQ0=sQuery(id+"F39.wireOp",EDGE,"E124.MirrorCS");Q2=makeQuery(id+"F39.imprint","IMPRINT",FACE,{"disambiguationData":[TD([[makeQuery(id+"F39.imprint","IMPRINT",EDGE,{"derivedFrom":subQ0}),1.0]])]});}
            var Q3;
            Q3=makeQuery(id+"F39.imprint","IMPRINT",FACE,{"disambiguationData":[TD([[makeQuery(id+"F39.imprint","IMPRINT",EDGE,{"derivedFrom":sQuery(id+"F39.wireOp",EDGE,"E112")}),-1.0]])]});
            var Q4;
            Q4=makeQuery(id+"F39.imprint","IMPRINT",FACE,{"disambiguationData":[TD([[makeQuery(id+"F39.imprint","IMPRINT",EDGE,{"derivedFrom":sQuery(id+"F39.wireOp",EDGE,"E115")}),1.0]])]});
            var Q5;
            {var subQ0=sQuery(id+"F39.wireOp",EDGE,"E126.MirrorCS");Q5=makeQuery(id+"F39.imprint","IMPRINT",FACE,{"disambiguationData":[TD([[makeQuery(id+"F39.imprint","IMPRINT",EDGE,{"derivedFrom":subQ0}),-1.0]])]});}
            var Q6;
            {var subQ5=sQuery(id+"F39.wireOp",EDGE,"E123.MirrorCS");Q6=makeQuery(id+"F39.imprint","IMPRINT",FACE,{"disambiguationData":[TD([[makeQuery(id+"F39.imprint","IMPRINT",EDGE,{"derivedFrom":subQ5}),-1.0]])]});}
            extrude(context, id + "F40", {"entities" : qUnion([Q0, Q1, Q2, Q3, Q4, Q5, Q6]), "operationType" : NewBodyOperationType.REMOVE, "endBound" : BoundingType.SYMMETRIC, "oppositeDirection" : true, "depth" : 60 * mm});
        }
        {
            var Q0;
            {var subQ1=sQuery(id+"F0.wireOp",EDGE,"E12.5");Q0=makeQuery(id+"F0.imprint","IMPRINT",FACE,{"disambiguationData":[TD([[makeQuery(id+"F0.imprint","IMPRINT",EDGE,{"derivedFrom":subQ1}),1.0]])]});}
            var Q1;
            {var subQ2=sQuery(id+"F0.wireOp",EDGE,"E12.0");Q1=makeQuery(id+"F0.imprint","IMPRINT",FACE,{"disambiguationData":[TD([[makeQuery(id+"F0.imprint","IMPRINT",EDGE,{"derivedFrom":subQ2}),-1.0]])]});}
            var Q2;
            {var subQ1=sQuery(id+"F0.wireOp",EDGE,"E3");Q2=makeQuery(id+"F0.imprint","IMPRINT",FACE,{"disambiguationData":[TD([[makeQuery(id+"F0.imprint","IMPRINT",EDGE,{"derivedFrom":subQ1}),1.0]])]});}
            var Q3;
            {var subQ3=sQuery(id+"F0.wireOp",EDGE,"E1.0");var subQ7=makeQuery(id+"F0.imprint","INTERSECT",VERTEX,{"derivedFrom":[subQ3,sQuery(id+"F0.wireOp",EDGE,"E11.MirrorCS")]});Q3=makeQuery(id+"F0.imprint","IMPRINT",FACE,{"disambiguationData":[TD([[makeQuery(id+"F0.imprint","IMPRINT",EDGE,{"disambiguationData":[TD([[subQ7,1.0]])],"derivedFrom":subQ3}),1.0]])]});}
            var Q4;
            Q4=makeQuery(id+"F0.imprint","IMPRINT",FACE,{"disambiguationData":[TD([[makeQuery(id+"F0.imprint","IMPRINT",EDGE,{"derivedFrom":sQuery(id+"F0.wireOp",EDGE,"E0")}),-1.0]])]});
            var Q5;
            {var subQ3=sQuery(id+"F0.wireOp",EDGE,"E1.0");var subQ5=makeQuery(id+"F0.imprint","INTERSECT",VERTEX,{"derivedFrom":[subQ3,sQuery(id+"F0.wireOp",EDGE,"E8.MirrorCS")]});Q5=makeQuery(id+"F0.imprint","IMPRINT",FACE,{"disambiguationData":[TD([[makeQuery(id+"F0.imprint","IMPRINT",EDGE,{"disambiguationData":[TD([[subQ5,-1.0]])],"derivedFrom":subQ3}),1.0]])]});}
            var Q6;
            {var subQ0=sQuery(id+"F0.wireOp",EDGE,"E9.MirrorCS");Q6=makeQuery(id+"F0.imprint","IMPRINT",FACE,{"disambiguationData":[TD([[makeQuery(id+"F0.imprint","IMPRINT",EDGE,{"derivedFrom":subQ0}),-1.0]])]});}
            extrude(context, id + "F41", {"entities" : qUnion([Q0, Q1, Q2, Q3, Q4, Q5, Q6]), "operationType" : NewBodyOperationType.ADD, "depth" : 153 * mm, "hasSecondDirection" : true, "secondDirectionOppositeDirection" : false, "secondDirectionDepth" : 150 * mm});
        }
        {
            var Q0;
            {var subQ1=sQuery(id+"F0.wireOp",EDGE,"E3");Q0=makeQuery(id+"F0.imprint","IMPRINT",FACE,{"disambiguationData":[TD([[makeQuery(id+"F0.imprint","IMPRINT",EDGE,{"derivedFrom":subQ1}),1.0]])]});}
            var Q1;
            {var subQ1=sQuery(id+"F0.wireOp",EDGE,"E12.5");Q1=makeQuery(id+"F0.imprint","IMPRINT",FACE,{"disambiguationData":[TD([[makeQuery(id+"F0.imprint","IMPRINT",EDGE,{"derivedFrom":subQ1}),1.0]])]});}
            var Q2;
            {var subQ3=sQuery(id+"F0.wireOp",EDGE,"E1.0");var subQ5=makeQuery(id+"F0.imprint","INTERSECT",VERTEX,{"derivedFrom":[subQ3,sQuery(id+"F0.wireOp",EDGE,"E8.MirrorCS")]});Q2=makeQuery(id+"F0.imprint","IMPRINT",FACE,{"disambiguationData":[TD([[makeQuery(id+"F0.imprint","IMPRINT",EDGE,{"disambiguationData":[TD([[subQ5,-1.0]])],"derivedFrom":subQ3}),1.0]])]});}
            var Q3;
            {var subQ3=sQuery(id+"F0.wireOp",EDGE,"E1.0");var subQ7=makeQuery(id+"F0.imprint","INTERSECT",VERTEX,{"derivedFrom":[subQ3,sQuery(id+"F0.wireOp",EDGE,"E11.MirrorCS")]});Q3=makeQuery(id+"F0.imprint","IMPRINT",FACE,{"disambiguationData":[TD([[makeQuery(id+"F0.imprint","IMPRINT",EDGE,{"disambiguationData":[TD([[subQ7,1.0]])],"derivedFrom":subQ3}),1.0]])]});}
            var Q4;
            {var subQ2=sQuery(id+"F0.wireOp",EDGE,"E12.0");Q4=makeQuery(id+"F0.imprint","IMPRINT",FACE,{"disambiguationData":[TD([[makeQuery(id+"F0.imprint","IMPRINT",EDGE,{"derivedFrom":subQ2}),-1.0]])]});}
            var Q5;
            {var subQ0=sQuery(id+"F0.wireOp",EDGE,"E9.MirrorCS");Q5=makeQuery(id+"F0.imprint","IMPRINT",FACE,{"disambiguationData":[TD([[makeQuery(id+"F0.imprint","IMPRINT",EDGE,{"derivedFrom":subQ0}),-1.0]])]});}
            var Q6;
            Q6=makeQuery(id+"F0.imprint","IMPRINT",FACE,{"disambiguationData":[TD([[makeQuery(id+"F0.imprint","IMPRINT",EDGE,{"derivedFrom":sQuery(id+"F0.wireOp",EDGE,"E0")}),-1.0]])]});
            extrude(context, id + "F42", {"entities" : qUnion([Q0, Q1, Q2, Q3, Q4, Q5, Q6]), "operationType" : NewBodyOperationType.ADD, "oppositeDirection" : true, "depth" : 3 * mm});
        }
        {
            var Q0;
            Q0=makeQuery(id+"F30.opExtrude","SWEPT_FACE",FACE,{"disambiguationData":[OSD([sQuery(id+"F18.wireOp",EDGE,"E51.bottom")])]});
            extrude(context, id + "F43", {"entities" : qUnion([Q0]), "depth" : 168 * mm});
        }
        {
            var Q0;
            Q0=qCreatedBy(makeId("Top.planeOp"),FACE);
            var sketch = newSketch(context, id + "F44", { "sketchPlane" : qUnion([Q0])});
            skLineSegment(sketch, "E128", {"start": v(1399.68, 0) * mm, "end": v(1533.77, 0) * mm, "construction": true});
            skLineSegment(sketch, "E129", {"start": v(1533.77, 0) * mm, "end": v(1533.77, 119.6) * mm, "construction": true});
            skLineSegment(sketch, "E130", {"start": v(1533.77, 0) * mm, "end": v(1533.77, -124.92) * mm, "construction": true});
            skLineSegment(sketch, "E131", {"start": v(1533.77, 0) * mm, "end": v(1599.16, 0) * mm, "construction": true});
            skCircle(sketch, "E132", {"center": v(1533.77, 0) * mm, "radius": 21.95 * mm});
            skCircle(sketch, "E133", {"center": v(1533.77, 0) * mm, "radius": 25 * mm});
            skSolve(sketch);
        }
        {
            var Q0;
            Q0=qCreatedBy(makeId("Front.planeOp"),FACE);
            var sketch = newSketch(context, id + "F45", { "sketchPlane" : qUnion([Q0])});
            skLineSegment(sketch, "E134", {"start": v(1533.77, 150) * mm, "end": v(1533.77, 125) * mm, "construction": true});
            skLineSegment(sketch, "E135", {"start": v(1533.77, 125) * mm, "end": v(1533.77, 25) * mm, "construction": true});
            skLineSegment(sketch, "E136", {"start": v(1533.77, 25) * mm, "end": v(1533.77, 0) * mm, "construction": true});
            skCircle(sketch, "E137", {"center": v(1533.77, 125) * mm, "radius": 17.5 * mm});
            skCircle(sketch, "E138", {"center": v(1533.77, 25) * mm, "radius": 17.5 * mm});
            skSolve(sketch);
        }
        {
            var Q0;
            Q0=makeQuery(id+"F45.imprint","IMPRINT",FACE,{"disambiguationData":[TD([[makeQuery(id+"F45.imprint","IMPRINT",EDGE,{"derivedFrom":sQuery(id+"F45.wireOp",EDGE,"E137")}),1.0]])]});
            var Q1;
            Q1=makeQuery(id+"F45.imprint","IMPRINT",FACE,{"disambiguationData":[TD([[makeQuery(id+"F45.imprint","IMPRINT",EDGE,{"derivedFrom":sQuery(id+"F45.wireOp",EDGE,"E138")}),1.0]])]});
            extrude(context, id + "F46", {"entities" : qUnion([Q0, Q1]), "endBound" : BoundingType.SYMMETRIC, "depth" : 25 * mm});
        }
    });
